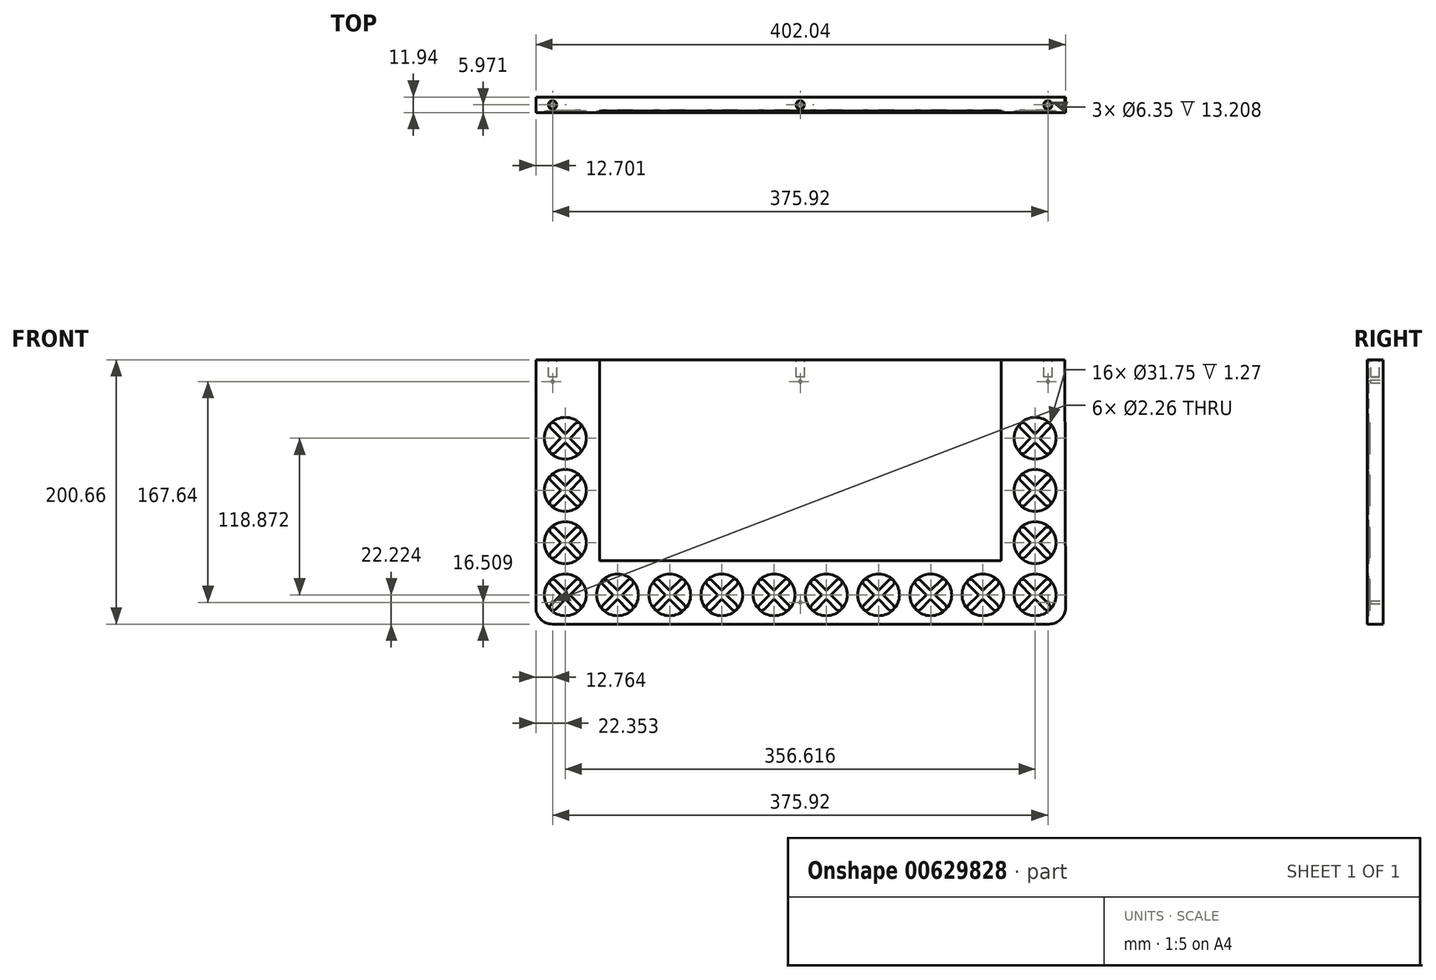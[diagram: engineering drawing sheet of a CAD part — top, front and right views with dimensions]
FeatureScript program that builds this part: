
annotation { "Feature Type Name" : "Feature", "Feature Type Description" : "" }
export const myFeature = defineFeature(function(context is Context, id is Id, definition is map)
    precondition{}
    {
        {
            var Q0;
            Q0=qCreatedBy(makeId("Front.planeOp"),FACE);
            var sketch = newSketch(context, id + "F0", { "sketchPlane" : qUnion([Q0])});
            skArc(sketch, "E0", {"start": v(-280, -77.67) * mm, "mid": v(-276.29, -86.65) * mm, "end": v(-267.3, -90.37) * mm});
            skArc(sketch, "E1", {"start": v(109.33, -90.37) * mm, "mid": v(118.3, -86.65) * mm, "end": v(122.03, -77.67) * mm});
            skLineSegment(sketch, "E2", {"start": v(121.31, 110.29) * mm, "end": v(122.03, -77.67) * mm});
            skLineSegment(sketch, "E3", {"start": v(109.33, -90.37) * mm, "end": v(-267.3, -90.37) * mm});
            skLineSegment(sketch, "E4", {"start": v(-280, 110.29) * mm, "end": v(-280, -77.67) * mm});
            skLineSegment(sketch, "E5", {"start": v(-280, 110.29) * mm, "end": v(121.31, 110.29) * mm});
            skSolve(sketch);
        }
        {
            var Q0;
            Q0=makeQuery(id+"F0.imprint","IMPRINT",FACE,{"disambiguationData":[TD([[makeQuery(id+"F0.imprint","IMPRINT",EDGE,{"derivedFrom":sQuery(id+"F0.wireOp",EDGE,"E0")}),1.0]])]});
            extrude(context, id + "F1", {"entities" : qUnion([Q0]), "depth" : 11.94 * mm, "offsetDistance" : 25.4 * mm});
        }
        {
            var Q0;
            Q0=makeQuery(id+"F1.opExtrude","SWEPT_FACE",FACE,{"disambiguationData":[OSD([sQuery(id+"F0.wireOp",EDGE,"E5")])]});
            var sketch = newSketch(context, id + "F2", { "sketchPlane" : qUnion([Q0])});
            skCircle(sketch, "E6", {"center": v(-267.3, -5.97) * mm, "radius": 3.18 * mm});
            skCircle(sketch, "E7", {"center": v(-79.35, -5.97) * mm, "radius": 3.18 * mm});
            skCircle(sketch, "E8", {"center": v(108.61, -5.97) * mm, "radius": 3.18 * mm});
            skSolve(sketch);
        }
        {
            var Q0;
            Q0=makeQuery(id+"F2.imprint","IMPRINT",FACE,{"disambiguationData":[TD([[makeQuery(id+"F2.imprint","IMPRINT",EDGE,{"derivedFrom":sQuery(id+"F2.wireOp",EDGE,"E6")}),1.0]])]});
            var Q1;
            Q1=makeQuery(id+"F2.imprint","IMPRINT",FACE,{"disambiguationData":[TD([[makeQuery(id+"F2.imprint","IMPRINT",EDGE,{"derivedFrom":sQuery(id+"F2.wireOp",EDGE,"E7")}),1.0]])]});
            var Q2;
            Q2=makeQuery(id+"F2.imprint","IMPRINT",FACE,{"disambiguationData":[TD([[makeQuery(id+"F2.imprint","IMPRINT",EDGE,{"derivedFrom":sQuery(id+"F2.wireOp",EDGE,"E8")}),1.0]])]});
            extrude(context, id + "F3", {"entities" : qUnion([Q0, Q1, Q2]), "operationType" : NewBodyOperationType.REMOVE, "oppositeDirection" : true, "depth" : 13.2 * mm, "offsetDistance" : 25.4 * mm});
        }
        {
            var Q0;
            Q0=makeQuery(id+"F1.opExtrude","CAP_FACE",FACE,{"disambiguationData":[OSD([sQuery(id+"F0.wireOp",EDGE,"E0"),sQuery(id+"F0.wireOp",EDGE,"E1"),sQuery(id+"F0.wireOp",EDGE,"E2"),sQuery(id+"F0.wireOp",EDGE,"E3"),sQuery(id+"F0.wireOp",EDGE,"E4"),sQuery(id+"F0.wireOp",EDGE,"E5")])],"isStart":true});
            var sketch = newSketch(context, id + "F4", { "sketchPlane" : qUnion([Q0])});
            skPoint(sketch, "E9", {"position": v(-108.67, 93.78) * mm});
            skPoint(sketch, "E10", {"position": v(267.25, -73.86) * mm});
            skPoint(sketch, "E11", {"position": v(79.29, 93.78) * mm});
            skPoint(sketch, "E12", {"position": v(-108.67, -73.86) * mm});
            skPoint(sketch, "E13", {"position": v(267.25, 93.78) * mm});
            skPoint(sketch, "E14", {"position": v(79.29, -73.86) * mm});
            skSolve(sketch);
        }
        {
            var Q0;
            Q0=sQuery(id+"F4.wireOp",VERTEX,"E9");
            var Q1;
            Q1=sQuery(id+"F4.wireOp",VERTEX,"E11");
            var Q2;
            Q2=sQuery(id+"F4.wireOp",VERTEX,"E13");
            var Q3;
            Q3=sQuery(id+"F4.wireOp",VERTEX,"E10");
            var Q4;
            Q4=sQuery(id+"F4.wireOp",VERTEX,"E14");
            var Q5;
            Q5=sQuery(id+"F4.wireOp",VERTEX,"E12");
            var Q6;
            Q6=makeQuery(id+"F1.opExtrude","SWEPT_BODY",BODY,{"disambiguationData":[OSD([sQuery(id+"F0.wireOp",EDGE,"E0"),sQuery(id+"F0.wireOp",EDGE,"E1"),sQuery(id+"F0.wireOp",EDGE,"E2"),sQuery(id+"F0.wireOp",EDGE,"E3"),sQuery(id+"F0.wireOp",EDGE,"E4"),sQuery(id+"F0.wireOp",EDGE,"E5")])]});
            hole(context, id + "F5", {"style" : HoleStyle.SIMPLE, "endStyle" : HoleEndStyle.BLIND, "standardTappedOrClearance" : lookupTablePath({ "standard" : "ANSI", "engagement" : "75%", "pitch" : "40 tpi", "size" : "#4", "type" : "Tapped" }), "standardBlindInLast" : lookupTablePath({ "standard" : "ANSI", "engagement" : "75%", "pitch" : "40 tpi", "size" : "#4", "type" : "Tapped" }), "holeDiameter" : 2.26 * mm, "showTappedDepth" : true, "holeDepth" : 9.52 * mm, "tappedDepth" : 7.62 * mm, "tapClearance" : 3, "locations" : qUnion([Q0, Q1, Q2, Q3, Q4, Q5]), "scope" : qUnion([Q6]), "majorDiameter" : 2.84 * mm});
        }
        {
            var Q0;
            Q0=makeQuery(id+"F1.opExtrude","CAP_FACE",FACE,{"disambiguationData":[OSD([sQuery(id+"F0.wireOp",EDGE,"E0"),sQuery(id+"F0.wireOp",EDGE,"E1"),sQuery(id+"F0.wireOp",EDGE,"E2"),sQuery(id+"F0.wireOp",EDGE,"E3"),sQuery(id+"F0.wireOp",EDGE,"E4"),sQuery(id+"F0.wireOp",EDGE,"E5")])],"isStart":false});
            var sketch = newSketch(context, id + "F6", { "sketchPlane" : qUnion([Q0])});
            skLineSegment(sketch, "E15.bottom", {"start": v(-231.75, 110.29) * mm, "end": v(73.05, 110.29) * mm});
            skArc(sketch, "E16", {"start": v(-231.75, -41.71) * mm, "mid": v(-231.63, -42) * mm, "end": v(-231.35, -42.11) * mm});
            skArc(sketch, "E17", {"start": v(72.65, -42.11) * mm, "mid": v(72.94, -42) * mm, "end": v(73.05, -41.71) * mm});
            skLineSegment(sketch, "E18", {"start": v(72.65, -42.11) * mm, "end": v(-231.35, -42.11) * mm});
            skLineSegment(sketch, "E19", {"start": v(-231.75, -41.71) * mm, "end": v(-231.75, 110.29) * mm});
            skLineSegment(sketch, "E20", {"start": v(73.05, 110.29) * mm, "end": v(73.05, -41.71) * mm});
            skSolve(sketch);
        }
        {
            var Q0;
            Q0=makeQuery(id+"F6.imprint","IMPRINT",FACE,{"disambiguationData":[TD([[makeQuery(id+"F6.imprint","IMPRINT",EDGE,{"derivedFrom":sQuery(id+"F6.wireOp",EDGE,"E15.bottom")}),-1.0]])]});
            extrude(context, id + "F7", {"entities" : qUnion([Q0]), "operationType" : NewBodyOperationType.REMOVE, "oppositeDirection" : true, "depth" : 1.27 * mm, "offsetDistance" : 25.4 * mm});
        }
        {
            var Q0;
            Q0=makeQuery(id+"F1.opExtrude","CAP_FACE",FACE,{"disambiguationData":[OSD([sQuery(id+"F0.wireOp",EDGE,"E0"),sQuery(id+"F0.wireOp",EDGE,"E1"),sQuery(id+"F0.wireOp",EDGE,"E2"),sQuery(id+"F0.wireOp",EDGE,"E3"),sQuery(id+"F0.wireOp",EDGE,"E4"),sQuery(id+"F0.wireOp",EDGE,"E5")])],"isStart":false});
            var sketch = newSketch(context, id + "F8", { "sketchPlane" : qUnion([Q0])});
            skCircle(sketch, "E21", {"center": v(-257.66, -68.15) * mm, "radius": 15.88 * mm});
            skCircle(sketch, "E22.1.0.0", {"center": v(-218.03, -68.15) * mm, "radius": 15.88 * mm});
            skCircle(sketch, "E22.2.0.0", {"center": v(-178.4, -68.15) * mm, "radius": 15.88 * mm});
            skCircle(sketch, "E22.3.0.0", {"center": v(-138.78, -68.15) * mm, "radius": 15.88 * mm});
            skCircle(sketch, "E22.4.0.0", {"center": v(-99.16, -68.15) * mm, "radius": 15.88 * mm});
            skCircle(sketch, "E22.5.0.0", {"center": v(-59.54, -68.15) * mm, "radius": 15.88 * mm});
            skCircle(sketch, "E22.6.0.0", {"center": v(-19.91, -68.15) * mm, "radius": 15.88 * mm});
            skCircle(sketch, "E22.7.0.0", {"center": v(19.71, -68.15) * mm, "radius": 15.88 * mm});
            skCircle(sketch, "E22.8.0.0", {"center": v(59.34, -68.15) * mm, "radius": 15.88 * mm});
            skCircle(sketch, "E22.9.0.0", {"center": v(98.96, -68.15) * mm, "radius": 15.88 * mm});
            skCircle(sketch, "E23.0.1.0", {"center": v(-257.66, -28.52) * mm, "radius": 15.88 * mm});
            skCircle(sketch, "E23.0.1.1", {"center": v(98.96, -28.52) * mm, "radius": 15.88 * mm});
            skCircle(sketch, "E23.0.2.0", {"center": v(-257.66, 11.1) * mm, "radius": 15.88 * mm});
            skCircle(sketch, "E23.0.2.1", {"center": v(98.96, 11.1) * mm, "radius": 15.88 * mm});
            skCircle(sketch, "E23.0.3.0", {"center": v(-257.66, 50.73) * mm, "radius": 15.88 * mm});
            skCircle(sketch, "E23.0.3.1", {"center": v(98.96, 50.73) * mm, "radius": 15.88 * mm});
            skSolve(sketch);
        }
        {
            var Q0;
            Q0=qSketchRegion(id+"F8",true);
            extrude(context, id + "F9", {"entities" : qUnion([Q0]), "operationType" : NewBodyOperationType.REMOVE, "oppositeDirection" : true, "depth" : 1.27 * mm, "offsetDistance" : 25.4 * mm});
        }
        {
            var Q0;
            Q0=makeQuery(id+"F1.opExtrude","CAP_FACE",FACE,{"disambiguationData":[OSD([sQuery(id+"F0.wireOp",EDGE,"E0"),sQuery(id+"F0.wireOp",EDGE,"E1"),sQuery(id+"F0.wireOp",EDGE,"E2"),sQuery(id+"F0.wireOp",EDGE,"E3"),sQuery(id+"F0.wireOp",EDGE,"E4"),sQuery(id+"F0.wireOp",EDGE,"E5")])],"isStart":false});
            var sketch = newSketch(context, id + "F10", { "sketchPlane" : qUnion([Q0])});
            skArc(sketch, "E24", {"start": v(-249.98, -79.24) * mm, "mid": v(-246.61, -79.37) * mm, "end": v(-246.48, -76) * mm});
            skArc(sketch, "E25", {"start": v(-265.42, -57.06) * mm, "mid": v(-268.8, -57.06) * mm, "end": v(-268.8, -60.42) * mm});
            skLineSegment(sketch, "E26.bottom", {"start": v(-254.2, -68.28) * mm, "end": v(-246.48, -60.56) * mm});
            skLineSegment(sketch, "E26.top", {"start": v(-257.7, -64.78) * mm, "end": v(-249.98, -57.06) * mm});
            skLineSegment(sketch, "E27.bottom", {"start": v(-257.7, -71.52) * mm, "end": v(-265.42, -79.24) * mm});
            skArc(sketch, "E28", {"start": v(-246.48, -60.56) * mm, "mid": v(-246.48, -57.06) * mm, "end": v(-249.98, -57.06) * mm});
            skArc(sketch, "E29", {"start": v(-268.8, -75.87) * mm, "mid": v(-268.8, -79.24) * mm, "end": v(-265.42, -79.24) * mm});
            skLineSegment(sketch, "E30.0", {"start": v(-249.98, -57.06) * mm, "end": v(-257.7, -64.78) * mm, "construction": true});
            skLineSegment(sketch, "E31", {"start": v(-268.8, -60.42) * mm, "end": v(-261.07, -68.15) * mm});
            skLineSegment(sketch, "E32", {"start": v(-265.42, -57.06) * mm, "end": v(-257.7, -64.78) * mm});
            skLineSegment(sketch, "E33", {"start": v(-254.2, -68.28) * mm, "end": v(-246.48, -76) * mm});
            skLineSegment(sketch, "E34", {"start": v(-249.98, -79.24) * mm, "end": v(-257.7, -71.52) * mm});
            skLineSegment(sketch, "E35", {"start": v(-261.07, -68.15) * mm, "end": v(-268.8, -75.87) * mm});
            skLineSegment(sketch, "E36.0", {"start": v(-251.89, -73.92) * mm, "end": v(-251.89, -73.92) * mm});
            skLineSegment(sketch, "E36.9", {"start": v(-251.89, -73.92) * mm, "end": v(-251.89, -73.92) * mm});
            skLineSegment(sketch, "E37.0", {"start": v(-257.7, -71.52) * mm, "end": v(-249.98, -79.24) * mm, "construction": true});
            skLineSegment(sketch, "E38.0", {"start": v(-254.2, -68.28) * mm, "end": v(-246.48, -76) * mm, "construction": true});
            skLineSegment(sketch, "E39.0", {"start": v(-268.8, -60.42) * mm, "end": v(-261.07, -68.15) * mm, "construction": true});
            skLineSegment(sketch, "E40.0", {"start": v(-265.42, -79.24) * mm, "end": v(-257.7, -71.52) * mm, "construction": true});
            skLineSegment(sketch, "E41.0", {"start": v(-268.8, -75.87) * mm, "end": v(-261.07, -68.15) * mm, "construction": true});
            skArc(sketch, "E42.0.0.1", {"start": v(-265.42, -17.43) * mm, "mid": v(-268.8, -17.43) * mm, "end": v(-268.8, -20.8) * mm});
            skLineSegment(sketch, "E42.4.0.1", {"start": v(-254.2, -28.66) * mm, "end": v(-246.48, -20.94) * mm});
            skLineSegment(sketch, "E42.7.0.1", {"start": v(-265.42, -17.43) * mm, "end": v(-257.7, -25.16) * mm});
            skLineSegment(sketch, "E42.10.0.1", {"start": v(-268.8, -36.25) * mm, "end": v(-261.07, -28.52) * mm, "construction": true});
            skLineSegment(sketch, "E42.13.0.1", {"start": v(-257.7, -31.9) * mm, "end": v(-249.98, -39.61) * mm, "construction": true});
            skLineSegment(sketch, "E42.16.0.1", {"start": v(-254.2, -28.66) * mm, "end": v(-246.48, -36.38) * mm, "construction": true});
            skLineSegment(sketch, "E42.19.0.1", {"start": v(-268.8, -20.8) * mm, "end": v(-261.07, -28.52) * mm, "construction": true});
            skArc(sketch, "E42.22.0.1", {"start": v(-249.98, -39.61) * mm, "mid": v(-246.61, -39.75) * mm, "end": v(-246.48, -36.38) * mm});
            skArc(sketch, "E42.26.0.1", {"start": v(-246.48, -20.94) * mm, "mid": v(-246.48, -17.43) * mm, "end": v(-249.98, -17.43) * mm});
            skLineSegment(sketch, "E42.30.0.1", {"start": v(-249.98, -17.43) * mm, "end": v(-257.7, -25.16) * mm, "construction": true});
            skLineSegment(sketch, "E42.33.0.1", {"start": v(-265.42, -39.61) * mm, "end": v(-257.7, -31.9) * mm, "construction": true});
            skLineSegment(sketch, "E42.36.0.1", {"start": v(-257.7, -25.16) * mm, "end": v(-249.98, -17.43) * mm});
            skArc(sketch, "E42.39.0.1", {"start": v(-268.8, -36.25) * mm, "mid": v(-268.8, -39.61) * mm, "end": v(-265.42, -39.61) * mm});
            skLineSegment(sketch, "E42.43.0.1", {"start": v(-268.8, -20.8) * mm, "end": v(-261.07, -28.52) * mm});
            skLineSegment(sketch, "E42.46.0.1", {"start": v(-254.2, -28.66) * mm, "end": v(-246.48, -36.38) * mm});
            skLineSegment(sketch, "E42.49.0.1", {"start": v(-249.98, -39.61) * mm, "end": v(-257.7, -31.9) * mm});
            skLineSegment(sketch, "E42.52.0.1", {"start": v(-261.07, -28.52) * mm, "end": v(-268.8, -36.25) * mm});
            skLineSegment(sketch, "E42.55.0.1", {"start": v(-257.7, -31.9) * mm, "end": v(-265.42, -39.61) * mm});
            skArc(sketch, "E42.0.0.2", {"start": v(-265.42, 22.2) * mm, "mid": v(-268.8, 22.2) * mm, "end": v(-268.8, 18.82) * mm});
            skLineSegment(sketch, "E42.4.0.2", {"start": v(-254.2, 10.97) * mm, "end": v(-246.48, 18.69) * mm});
            skLineSegment(sketch, "E42.7.0.2", {"start": v(-265.42, 22.2) * mm, "end": v(-257.7, 14.47) * mm});
            skLineSegment(sketch, "E42.10.0.2", {"start": v(-268.8, 3.38) * mm, "end": v(-261.07, 11.1) * mm, "construction": true});
            skLineSegment(sketch, "E42.13.0.2", {"start": v(-257.7, 7.73) * mm, "end": v(-249.98, 0) * mm, "construction": true});
            skLineSegment(sketch, "E42.16.0.2", {"start": v(-254.2, 10.97) * mm, "end": v(-246.48, 3.24) * mm, "construction": true});
            skLineSegment(sketch, "E42.19.0.2", {"start": v(-268.8, 18.82) * mm, "end": v(-261.07, 11.1) * mm, "construction": true});
            skArc(sketch, "E42.22.0.2", {"start": v(-249.98, 0) * mm, "mid": v(-246.61, -0.13) * mm, "end": v(-246.48, 3.24) * mm});
            skArc(sketch, "E42.26.0.2", {"start": v(-246.48, 18.69) * mm, "mid": v(-246.48, 22.2) * mm, "end": v(-249.98, 22.2) * mm});
            skLineSegment(sketch, "E42.30.0.2", {"start": v(-249.98, 22.2) * mm, "end": v(-257.7, 14.47) * mm, "construction": true});
            skLineSegment(sketch, "E42.33.0.2", {"start": v(-265.42, 0) * mm, "end": v(-257.7, 7.73) * mm, "construction": true});
            skLineSegment(sketch, "E42.36.0.2", {"start": v(-257.7, 14.47) * mm, "end": v(-249.98, 22.2) * mm});
            skArc(sketch, "E42.39.0.2", {"start": v(-268.8, 3.38) * mm, "mid": v(-268.8, 0) * mm, "end": v(-265.42, 0) * mm});
            skLineSegment(sketch, "E42.43.0.2", {"start": v(-268.8, 18.82) * mm, "end": v(-261.07, 11.1) * mm});
            skLineSegment(sketch, "E42.46.0.2", {"start": v(-254.2, 10.97) * mm, "end": v(-246.48, 3.24) * mm});
            skLineSegment(sketch, "E42.49.0.2", {"start": v(-249.98, 0) * mm, "end": v(-257.7, 7.73) * mm});
            skLineSegment(sketch, "E42.52.0.2", {"start": v(-261.07, 11.1) * mm, "end": v(-268.8, 3.38) * mm});
            skLineSegment(sketch, "E42.55.0.2", {"start": v(-257.7, 7.73) * mm, "end": v(-265.42, 0) * mm});
            skArc(sketch, "E42.0.0.3", {"start": v(-265.42, 61.81) * mm, "mid": v(-268.8, 61.81) * mm, "end": v(-268.8, 58.45) * mm});
            skLineSegment(sketch, "E42.4.0.3", {"start": v(-254.2, 50.59) * mm, "end": v(-246.48, 58.31) * mm});
            skLineSegment(sketch, "E42.7.0.3", {"start": v(-265.42, 61.81) * mm, "end": v(-257.7, 54.1) * mm});
            skLineSegment(sketch, "E42.10.0.3", {"start": v(-268.8, 43) * mm, "end": v(-261.07, 50.72) * mm, "construction": true});
            skLineSegment(sketch, "E42.13.0.3", {"start": v(-257.7, 47.36) * mm, "end": v(-249.98, 39.63) * mm, "construction": true});
            skLineSegment(sketch, "E42.16.0.3", {"start": v(-254.2, 50.59) * mm, "end": v(-246.48, 42.87) * mm, "construction": true});
            skLineSegment(sketch, "E42.19.0.3", {"start": v(-268.8, 58.45) * mm, "end": v(-261.07, 50.72) * mm, "construction": true});
            skArc(sketch, "E42.22.0.3", {"start": v(-249.98, 39.63) * mm, "mid": v(-246.61, 39.5) * mm, "end": v(-246.48, 42.87) * mm});
            skArc(sketch, "E42.26.0.3", {"start": v(-246.48, 58.31) * mm, "mid": v(-246.48, 61.81) * mm, "end": v(-249.98, 61.81) * mm});
            skLineSegment(sketch, "E42.30.0.3", {"start": v(-249.98, 61.81) * mm, "end": v(-257.7, 54.1) * mm, "construction": true});
            skLineSegment(sketch, "E42.33.0.3", {"start": v(-265.42, 39.63) * mm, "end": v(-257.7, 47.36) * mm, "construction": true});
            skLineSegment(sketch, "E42.36.0.3", {"start": v(-257.7, 54.1) * mm, "end": v(-249.98, 61.81) * mm});
            skArc(sketch, "E42.39.0.3", {"start": v(-268.8, 43) * mm, "mid": v(-268.8, 39.63) * mm, "end": v(-265.42, 39.63) * mm});
            skLineSegment(sketch, "E42.43.0.3", {"start": v(-268.8, 58.45) * mm, "end": v(-261.07, 50.72) * mm});
            skLineSegment(sketch, "E42.46.0.3", {"start": v(-254.2, 50.59) * mm, "end": v(-246.48, 42.87) * mm});
            skLineSegment(sketch, "E42.49.0.3", {"start": v(-249.98, 39.63) * mm, "end": v(-257.7, 47.36) * mm});
            skLineSegment(sketch, "E42.52.0.3", {"start": v(-261.07, 50.72) * mm, "end": v(-268.8, 43) * mm});
            skLineSegment(sketch, "E42.55.0.3", {"start": v(-257.7, 47.36) * mm, "end": v(-265.42, 39.63) * mm});
            skArc(sketch, "E43.0.1.0", {"start": v(-229.17, -75.87) * mm, "mid": v(-229.17, -79.24) * mm, "end": v(-225.8, -79.24) * mm});
            skArc(sketch, "E43.4.1.0", {"start": v(-225.8, -57.06) * mm, "mid": v(-229.17, -57.06) * mm, "end": v(-229.17, -60.42) * mm});
            skLineSegment(sketch, "E43.8.1.0", {"start": v(-214.57, -68.28) * mm, "end": v(-206.85, -76) * mm, "construction": true});
            skLineSegment(sketch, "E43.11.1.0", {"start": v(-218.08, -71.52) * mm, "end": v(-210.35, -79.24) * mm, "construction": true});
            skLineSegment(sketch, "E43.14.1.0", {"start": v(-225.8, -79.24) * mm, "end": v(-218.08, -71.52) * mm, "construction": true});
            skArc(sketch, "E43.17.1.0", {"start": v(-210.35, -79.24) * mm, "mid": v(-206.99, -79.37) * mm, "end": v(-206.85, -76) * mm});
            skArc(sketch, "E43.21.1.0", {"start": v(-206.85, -60.56) * mm, "mid": v(-206.85, -57.06) * mm, "end": v(-210.35, -57.06) * mm});
            skLineSegment(sketch, "E43.25.1.0", {"start": v(-214.57, -68.28) * mm, "end": v(-206.85, -60.56) * mm});
            skLineSegment(sketch, "E43.28.1.0", {"start": v(-229.17, -75.87) * mm, "end": v(-221.44, -68.15) * mm, "construction": true});
            skLineSegment(sketch, "E43.31.1.0", {"start": v(-229.17, -60.42) * mm, "end": v(-221.44, -68.15) * mm, "construction": true});
            skLineSegment(sketch, "E43.34.1.0", {"start": v(-225.8, -57.06) * mm, "end": v(-218.08, -64.78) * mm});
            skLineSegment(sketch, "E43.37.1.0", {"start": v(-210.35, -57.06) * mm, "end": v(-218.08, -64.78) * mm, "construction": true});
            skLineSegment(sketch, "E43.40.1.0", {"start": v(-210.35, -79.24) * mm, "end": v(-218.08, -71.52) * mm});
            skLineSegment(sketch, "E43.43.1.0", {"start": v(-214.57, -68.28) * mm, "end": v(-206.85, -76) * mm});
            skLineSegment(sketch, "E43.46.1.0", {"start": v(-218.08, -64.78) * mm, "end": v(-210.35, -57.06) * mm});
            skLineSegment(sketch, "E43.49.1.0", {"start": v(-221.44, -68.15) * mm, "end": v(-229.17, -75.87) * mm});
            skLineSegment(sketch, "E43.52.1.0", {"start": v(-229.17, -60.42) * mm, "end": v(-221.44, -68.15) * mm});
            skLineSegment(sketch, "E43.55.1.0", {"start": v(-218.08, -71.52) * mm, "end": v(-225.8, -79.24) * mm});
            skArc(sketch, "E43.0.2.0", {"start": v(-189.54, -75.87) * mm, "mid": v(-189.54, -79.24) * mm, "end": v(-186.18, -79.24) * mm});
            skArc(sketch, "E43.4.2.0", {"start": v(-186.18, -57.06) * mm, "mid": v(-189.54, -57.06) * mm, "end": v(-189.54, -60.42) * mm});
            skLineSegment(sketch, "E43.8.2.0", {"start": v(-174.95, -68.28) * mm, "end": v(-167.23, -76) * mm, "construction": true});
            skLineSegment(sketch, "E43.11.2.0", {"start": v(-178.45, -71.52) * mm, "end": v(-170.73, -79.24) * mm, "construction": true});
            skLineSegment(sketch, "E43.14.2.0", {"start": v(-186.18, -79.24) * mm, "end": v(-178.45, -71.52) * mm, "construction": true});
            skArc(sketch, "E43.17.2.0", {"start": v(-170.73, -79.24) * mm, "mid": v(-167.36, -79.37) * mm, "end": v(-167.23, -76) * mm});
            skArc(sketch, "E43.21.2.0", {"start": v(-167.23, -60.56) * mm, "mid": v(-167.23, -57.06) * mm, "end": v(-170.73, -57.06) * mm});
            skLineSegment(sketch, "E43.25.2.0", {"start": v(-174.95, -68.28) * mm, "end": v(-167.23, -60.56) * mm});
            skLineSegment(sketch, "E43.28.2.0", {"start": v(-189.54, -75.87) * mm, "end": v(-181.82, -68.15) * mm, "construction": true});
            skLineSegment(sketch, "E43.31.2.0", {"start": v(-189.54, -60.42) * mm, "end": v(-181.82, -68.15) * mm, "construction": true});
            skLineSegment(sketch, "E43.34.2.0", {"start": v(-186.18, -57.06) * mm, "end": v(-178.45, -64.78) * mm});
            skLineSegment(sketch, "E43.37.2.0", {"start": v(-170.73, -57.06) * mm, "end": v(-178.45, -64.78) * mm, "construction": true});
            skLineSegment(sketch, "E43.40.2.0", {"start": v(-170.73, -79.24) * mm, "end": v(-178.45, -71.52) * mm});
            skLineSegment(sketch, "E43.43.2.0", {"start": v(-174.95, -68.28) * mm, "end": v(-167.23, -76) * mm});
            skLineSegment(sketch, "E43.46.2.0", {"start": v(-178.45, -64.78) * mm, "end": v(-170.73, -57.06) * mm});
            skLineSegment(sketch, "E43.49.2.0", {"start": v(-181.82, -68.15) * mm, "end": v(-189.54, -75.87) * mm});
            skLineSegment(sketch, "E43.52.2.0", {"start": v(-189.54, -60.42) * mm, "end": v(-181.82, -68.15) * mm});
            skLineSegment(sketch, "E43.55.2.0", {"start": v(-178.45, -71.52) * mm, "end": v(-186.18, -79.24) * mm});
            skArc(sketch, "E43.0.3.0", {"start": v(-149.92, -75.87) * mm, "mid": v(-149.92, -79.24) * mm, "end": v(-146.55, -79.24) * mm});
            skArc(sketch, "E43.4.3.0", {"start": v(-146.55, -57.06) * mm, "mid": v(-149.92, -57.06) * mm, "end": v(-149.92, -60.42) * mm});
            skLineSegment(sketch, "E43.8.3.0", {"start": v(-135.33, -68.28) * mm, "end": v(-127.6, -76) * mm, "construction": true});
            skLineSegment(sketch, "E43.11.3.0", {"start": v(-138.83, -71.52) * mm, "end": v(-131.1, -79.24) * mm, "construction": true});
            skLineSegment(sketch, "E43.14.3.0", {"start": v(-146.55, -79.24) * mm, "end": v(-138.83, -71.52) * mm, "construction": true});
            skArc(sketch, "E43.17.3.0", {"start": v(-131.1, -79.24) * mm, "mid": v(-127.74, -79.37) * mm, "end": v(-127.6, -76) * mm});
            skArc(sketch, "E43.21.3.0", {"start": v(-127.6, -60.56) * mm, "mid": v(-127.6, -57.06) * mm, "end": v(-131.1, -57.06) * mm});
            skLineSegment(sketch, "E43.25.3.0", {"start": v(-135.33, -68.28) * mm, "end": v(-127.6, -60.56) * mm});
            skLineSegment(sketch, "E43.28.3.0", {"start": v(-149.92, -75.87) * mm, "end": v(-142.2, -68.15) * mm, "construction": true});
            skLineSegment(sketch, "E43.31.3.0", {"start": v(-149.92, -60.42) * mm, "end": v(-142.2, -68.15) * mm, "construction": true});
            skLineSegment(sketch, "E43.34.3.0", {"start": v(-146.55, -57.06) * mm, "end": v(-138.83, -64.78) * mm});
            skLineSegment(sketch, "E43.37.3.0", {"start": v(-131.1, -57.06) * mm, "end": v(-138.83, -64.78) * mm, "construction": true});
            skLineSegment(sketch, "E43.40.3.0", {"start": v(-131.1, -79.24) * mm, "end": v(-138.83, -71.52) * mm});
            skLineSegment(sketch, "E43.43.3.0", {"start": v(-135.33, -68.28) * mm, "end": v(-127.6, -76) * mm});
            skLineSegment(sketch, "E43.46.3.0", {"start": v(-138.83, -64.78) * mm, "end": v(-131.1, -57.06) * mm});
            skLineSegment(sketch, "E43.49.3.0", {"start": v(-142.2, -68.15) * mm, "end": v(-149.92, -75.87) * mm});
            skLineSegment(sketch, "E43.52.3.0", {"start": v(-149.92, -60.42) * mm, "end": v(-142.2, -68.15) * mm});
            skLineSegment(sketch, "E43.55.3.0", {"start": v(-138.83, -71.52) * mm, "end": v(-146.55, -79.24) * mm});
            skArc(sketch, "E43.0.4.0", {"start": v(-110.3, -75.87) * mm, "mid": v(-110.3, -79.24) * mm, "end": v(-106.93, -79.24) * mm});
            skArc(sketch, "E43.4.4.0", {"start": v(-106.93, -57.06) * mm, "mid": v(-110.3, -57.06) * mm, "end": v(-110.3, -60.42) * mm});
            skLineSegment(sketch, "E43.8.4.0", {"start": v(-95.7, -68.28) * mm, "end": v(-87.98, -76) * mm, "construction": true});
            skLineSegment(sketch, "E43.11.4.0", {"start": v(-99.2, -71.52) * mm, "end": v(-91.48, -79.24) * mm, "construction": true});
            skLineSegment(sketch, "E43.14.4.0", {"start": v(-106.93, -79.24) * mm, "end": v(-99.2, -71.52) * mm, "construction": true});
            skArc(sketch, "E43.17.4.0", {"start": v(-91.48, -79.24) * mm, "mid": v(-88.11, -79.37) * mm, "end": v(-87.98, -76) * mm});
            skArc(sketch, "E43.21.4.0", {"start": v(-87.98, -60.56) * mm, "mid": v(-87.98, -57.06) * mm, "end": v(-91.48, -57.06) * mm});
            skLineSegment(sketch, "E43.25.4.0", {"start": v(-95.7, -68.28) * mm, "end": v(-87.98, -60.56) * mm});
            skLineSegment(sketch, "E43.28.4.0", {"start": v(-110.3, -75.87) * mm, "end": v(-102.57, -68.15) * mm, "construction": true});
            skLineSegment(sketch, "E43.31.4.0", {"start": v(-110.3, -60.42) * mm, "end": v(-102.57, -68.15) * mm, "construction": true});
            skLineSegment(sketch, "E43.34.4.0", {"start": v(-106.93, -57.06) * mm, "end": v(-99.2, -64.78) * mm});
            skLineSegment(sketch, "E43.37.4.0", {"start": v(-91.48, -57.06) * mm, "end": v(-99.2, -64.78) * mm, "construction": true});
            skLineSegment(sketch, "E43.40.4.0", {"start": v(-91.48, -79.24) * mm, "end": v(-99.2, -71.52) * mm});
            skLineSegment(sketch, "E43.43.4.0", {"start": v(-95.7, -68.28) * mm, "end": v(-87.98, -76) * mm});
            skLineSegment(sketch, "E43.46.4.0", {"start": v(-99.2, -64.78) * mm, "end": v(-91.48, -57.06) * mm});
            skLineSegment(sketch, "E43.49.4.0", {"start": v(-102.57, -68.15) * mm, "end": v(-110.3, -75.87) * mm});
            skLineSegment(sketch, "E43.52.4.0", {"start": v(-110.3, -60.42) * mm, "end": v(-102.57, -68.15) * mm});
            skLineSegment(sketch, "E43.55.4.0", {"start": v(-99.2, -71.52) * mm, "end": v(-106.93, -79.24) * mm});
            skArc(sketch, "E43.0.5.0", {"start": v(-70.67, -75.87) * mm, "mid": v(-70.67, -79.24) * mm, "end": v(-67.3, -79.24) * mm});
            skArc(sketch, "E43.4.5.0", {"start": v(-67.3, -57.06) * mm, "mid": v(-70.67, -57.06) * mm, "end": v(-70.67, -60.42) * mm});
            skLineSegment(sketch, "E43.8.5.0", {"start": v(-56.08, -68.28) * mm, "end": v(-48.36, -76) * mm, "construction": true});
            skLineSegment(sketch, "E43.11.5.0", {"start": v(-59.58, -71.52) * mm, "end": v(-51.86, -79.24) * mm, "construction": true});
            skLineSegment(sketch, "E43.14.5.0", {"start": v(-67.3, -79.24) * mm, "end": v(-59.58, -71.52) * mm, "construction": true});
            skArc(sketch, "E43.17.5.0", {"start": v(-51.86, -79.24) * mm, "mid": v(-48.5, -79.37) * mm, "end": v(-48.36, -76) * mm});
            skArc(sketch, "E43.21.5.0", {"start": v(-48.36, -60.56) * mm, "mid": v(-48.36, -57.06) * mm, "end": v(-51.86, -57.06) * mm});
            skLineSegment(sketch, "E43.25.5.0", {"start": v(-56.08, -68.28) * mm, "end": v(-48.36, -60.56) * mm});
            skLineSegment(sketch, "E43.28.5.0", {"start": v(-70.67, -75.87) * mm, "end": v(-62.95, -68.15) * mm, "construction": true});
            skLineSegment(sketch, "E43.31.5.0", {"start": v(-70.67, -60.42) * mm, "end": v(-62.95, -68.15) * mm, "construction": true});
            skLineSegment(sketch, "E43.34.5.0", {"start": v(-67.3, -57.06) * mm, "end": v(-59.58, -64.78) * mm});
            skLineSegment(sketch, "E43.37.5.0", {"start": v(-51.86, -57.06) * mm, "end": v(-59.58, -64.78) * mm, "construction": true});
            skLineSegment(sketch, "E43.40.5.0", {"start": v(-51.86, -79.24) * mm, "end": v(-59.58, -71.52) * mm});
            skLineSegment(sketch, "E43.43.5.0", {"start": v(-56.08, -68.28) * mm, "end": v(-48.36, -76) * mm});
            skLineSegment(sketch, "E43.46.5.0", {"start": v(-59.58, -64.78) * mm, "end": v(-51.86, -57.06) * mm});
            skLineSegment(sketch, "E43.49.5.0", {"start": v(-62.95, -68.15) * mm, "end": v(-70.67, -75.87) * mm});
            skLineSegment(sketch, "E43.52.5.0", {"start": v(-70.67, -60.42) * mm, "end": v(-62.95, -68.15) * mm});
            skLineSegment(sketch, "E43.55.5.0", {"start": v(-59.58, -71.52) * mm, "end": v(-67.3, -79.24) * mm});
            skArc(sketch, "E43.0.6.0", {"start": v(-31.05, -75.87) * mm, "mid": v(-31.05, -79.24) * mm, "end": v(-27.68, -79.24) * mm});
            skArc(sketch, "E43.4.6.0", {"start": v(-27.68, -57.06) * mm, "mid": v(-31.05, -57.06) * mm, "end": v(-31.05, -60.42) * mm});
            skLineSegment(sketch, "E43.8.6.0", {"start": v(-16.45, -68.28) * mm, "end": v(-8.73, -76) * mm, "construction": true});
            skLineSegment(sketch, "E43.11.6.0", {"start": v(-19.96, -71.52) * mm, "end": v(-12.23, -79.24) * mm, "construction": true});
            skLineSegment(sketch, "E43.14.6.0", {"start": v(-27.68, -79.24) * mm, "end": v(-19.96, -71.52) * mm, "construction": true});
            skArc(sketch, "E43.17.6.0", {"start": v(-12.23, -79.24) * mm, "mid": v(-8.87, -79.37) * mm, "end": v(-8.73, -76) * mm});
            skArc(sketch, "E43.21.6.0", {"start": v(-8.73, -60.56) * mm, "mid": v(-8.73, -57.06) * mm, "end": v(-12.23, -57.06) * mm});
            skLineSegment(sketch, "E43.25.6.0", {"start": v(-16.45, -68.28) * mm, "end": v(-8.73, -60.56) * mm});
            skLineSegment(sketch, "E43.28.6.0", {"start": v(-31.05, -75.87) * mm, "end": v(-23.32, -68.15) * mm, "construction": true});
            skLineSegment(sketch, "E43.31.6.0", {"start": v(-31.05, -60.42) * mm, "end": v(-23.32, -68.15) * mm, "construction": true});
            skLineSegment(sketch, "E43.34.6.0", {"start": v(-27.68, -57.06) * mm, "end": v(-19.96, -64.78) * mm});
            skLineSegment(sketch, "E43.37.6.0", {"start": v(-12.23, -57.06) * mm, "end": v(-19.96, -64.78) * mm, "construction": true});
            skLineSegment(sketch, "E43.40.6.0", {"start": v(-12.23, -79.24) * mm, "end": v(-19.96, -71.52) * mm});
            skLineSegment(sketch, "E43.43.6.0", {"start": v(-16.45, -68.28) * mm, "end": v(-8.73, -76) * mm});
            skLineSegment(sketch, "E43.46.6.0", {"start": v(-19.96, -64.78) * mm, "end": v(-12.23, -57.06) * mm});
            skLineSegment(sketch, "E43.49.6.0", {"start": v(-23.32, -68.15) * mm, "end": v(-31.05, -75.87) * mm});
            skLineSegment(sketch, "E43.52.6.0", {"start": v(-31.05, -60.42) * mm, "end": v(-23.32, -68.15) * mm});
            skLineSegment(sketch, "E43.55.6.0", {"start": v(-19.96, -71.52) * mm, "end": v(-27.68, -79.24) * mm});
            skArc(sketch, "E43.0.7.0", {"start": v(8.58, -75.87) * mm, "mid": v(8.58, -79.24) * mm, "end": v(11.94, -79.24) * mm});
            skArc(sketch, "E43.4.7.0", {"start": v(11.94, -57.06) * mm, "mid": v(8.58, -57.06) * mm, "end": v(8.58, -60.42) * mm});
            skLineSegment(sketch, "E43.8.7.0", {"start": v(23.17, -68.28) * mm, "end": v(30.9, -76) * mm, "construction": true});
            skLineSegment(sketch, "E43.11.7.0", {"start": v(19.67, -71.52) * mm, "end": v(27.39, -79.24) * mm, "construction": true});
            skLineSegment(sketch, "E43.14.7.0", {"start": v(11.94, -79.24) * mm, "end": v(19.67, -71.52) * mm, "construction": true});
            skArc(sketch, "E43.17.7.0", {"start": v(27.39, -79.24) * mm, "mid": v(30.76, -79.37) * mm, "end": v(30.9, -76) * mm});
            skArc(sketch, "E43.21.7.0", {"start": v(30.9, -60.56) * mm, "mid": v(30.9, -57.06) * mm, "end": v(27.39, -57.06) * mm});
            skLineSegment(sketch, "E43.25.7.0", {"start": v(23.17, -68.28) * mm, "end": v(30.9, -60.56) * mm});
            skLineSegment(sketch, "E43.28.7.0", {"start": v(8.58, -75.87) * mm, "end": v(16.3, -68.15) * mm, "construction": true});
            skLineSegment(sketch, "E43.31.7.0", {"start": v(8.58, -60.42) * mm, "end": v(16.3, -68.15) * mm, "construction": true});
            skLineSegment(sketch, "E43.34.7.0", {"start": v(11.94, -57.06) * mm, "end": v(19.67, -64.78) * mm});
            skLineSegment(sketch, "E43.37.7.0", {"start": v(27.39, -57.06) * mm, "end": v(19.67, -64.78) * mm, "construction": true});
            skLineSegment(sketch, "E43.40.7.0", {"start": v(27.39, -79.24) * mm, "end": v(19.67, -71.52) * mm});
            skLineSegment(sketch, "E43.43.7.0", {"start": v(23.17, -68.28) * mm, "end": v(30.9, -76) * mm});
            skLineSegment(sketch, "E43.46.7.0", {"start": v(19.67, -64.78) * mm, "end": v(27.39, -57.06) * mm});
            skLineSegment(sketch, "E43.49.7.0", {"start": v(16.3, -68.15) * mm, "end": v(8.58, -75.87) * mm});
            skLineSegment(sketch, "E43.52.7.0", {"start": v(8.58, -60.42) * mm, "end": v(16.3, -68.15) * mm});
            skLineSegment(sketch, "E43.55.7.0", {"start": v(19.67, -71.52) * mm, "end": v(11.94, -79.24) * mm});
            skArc(sketch, "E43.0.8.0", {"start": v(48.2, -75.87) * mm, "mid": v(48.2, -79.24) * mm, "end": v(51.57, -79.24) * mm});
            skArc(sketch, "E43.4.8.0", {"start": v(51.57, -57.06) * mm, "mid": v(48.2, -57.06) * mm, "end": v(48.2, -60.42) * mm});
            skLineSegment(sketch, "E43.8.8.0", {"start": v(62.8, -68.28) * mm, "end": v(70.52, -76) * mm, "construction": true});
            skLineSegment(sketch, "E43.11.8.0", {"start": v(59.3, -71.52) * mm, "end": v(67.01, -79.24) * mm, "construction": true});
            skLineSegment(sketch, "E43.14.8.0", {"start": v(51.57, -79.24) * mm, "end": v(59.3, -71.52) * mm, "construction": true});
            skArc(sketch, "E43.17.8.0", {"start": v(67.01, -79.24) * mm, "mid": v(70.38, -79.37) * mm, "end": v(70.52, -76) * mm});
            skArc(sketch, "E43.21.8.0", {"start": v(70.52, -60.56) * mm, "mid": v(70.52, -57.06) * mm, "end": v(67.01, -57.06) * mm});
            skLineSegment(sketch, "E43.25.8.0", {"start": v(62.8, -68.28) * mm, "end": v(70.52, -60.56) * mm});
            skLineSegment(sketch, "E43.28.8.0", {"start": v(48.2, -75.87) * mm, "end": v(55.92, -68.15) * mm, "construction": true});
            skLineSegment(sketch, "E43.31.8.0", {"start": v(48.2, -60.42) * mm, "end": v(55.92, -68.15) * mm, "construction": true});
            skLineSegment(sketch, "E43.34.8.0", {"start": v(51.57, -57.06) * mm, "end": v(59.3, -64.78) * mm});
            skLineSegment(sketch, "E43.37.8.0", {"start": v(67.01, -57.06) * mm, "end": v(59.3, -64.78) * mm, "construction": true});
            skLineSegment(sketch, "E43.40.8.0", {"start": v(67.01, -79.24) * mm, "end": v(59.3, -71.52) * mm});
            skLineSegment(sketch, "E43.43.8.0", {"start": v(62.8, -68.28) * mm, "end": v(70.52, -76) * mm});
            skLineSegment(sketch, "E43.46.8.0", {"start": v(59.3, -64.78) * mm, "end": v(67.01, -57.06) * mm});
            skLineSegment(sketch, "E43.49.8.0", {"start": v(55.92, -68.15) * mm, "end": v(48.2, -75.87) * mm});
            skLineSegment(sketch, "E43.52.8.0", {"start": v(48.2, -60.42) * mm, "end": v(55.92, -68.15) * mm});
            skLineSegment(sketch, "E43.55.8.0", {"start": v(59.3, -71.52) * mm, "end": v(51.57, -79.24) * mm});
            skArc(sketch, "E43.0.9.0", {"start": v(87.82, -75.87) * mm, "mid": v(87.82, -79.24) * mm, "end": v(91.2, -79.24) * mm});
            skArc(sketch, "E43.4.9.0", {"start": v(91.2, -57.06) * mm, "mid": v(87.82, -57.06) * mm, "end": v(87.82, -60.42) * mm});
            skLineSegment(sketch, "E43.8.9.0", {"start": v(102.42, -68.28) * mm, "end": v(110.14, -76) * mm, "construction": true});
            skLineSegment(sketch, "E43.11.9.0", {"start": v(98.91, -71.52) * mm, "end": v(106.64, -79.24) * mm, "construction": true});
            skLineSegment(sketch, "E43.14.9.0", {"start": v(91.2, -79.24) * mm, "end": v(98.91, -71.52) * mm, "construction": true});
            skArc(sketch, "E43.17.9.0", {"start": v(106.64, -79.24) * mm, "mid": v(110, -79.37) * mm, "end": v(110.14, -76) * mm});
            skArc(sketch, "E43.21.9.0", {"start": v(110.14, -60.56) * mm, "mid": v(110.14, -57.06) * mm, "end": v(106.64, -57.06) * mm});
            skLineSegment(sketch, "E43.25.9.0", {"start": v(102.42, -68.28) * mm, "end": v(110.14, -60.56) * mm});
            skLineSegment(sketch, "E43.28.9.0", {"start": v(87.82, -75.87) * mm, "end": v(95.55, -68.15) * mm, "construction": true});
            skLineSegment(sketch, "E43.31.9.0", {"start": v(87.82, -60.42) * mm, "end": v(95.55, -68.15) * mm, "construction": true});
            skLineSegment(sketch, "E43.34.9.0", {"start": v(91.2, -57.06) * mm, "end": v(98.91, -64.78) * mm});
            skLineSegment(sketch, "E43.37.9.0", {"start": v(106.64, -57.06) * mm, "end": v(98.91, -64.78) * mm, "construction": true});
            skLineSegment(sketch, "E43.40.9.0", {"start": v(106.64, -79.24) * mm, "end": v(98.91, -71.52) * mm});
            skLineSegment(sketch, "E43.43.9.0", {"start": v(102.42, -68.28) * mm, "end": v(110.14, -76) * mm});
            skLineSegment(sketch, "E43.46.9.0", {"start": v(98.91, -64.78) * mm, "end": v(106.64, -57.06) * mm});
            skLineSegment(sketch, "E43.49.9.0", {"start": v(95.55, -68.15) * mm, "end": v(87.82, -75.87) * mm});
            skLineSegment(sketch, "E43.52.9.0", {"start": v(87.82, -60.42) * mm, "end": v(95.55, -68.15) * mm});
            skLineSegment(sketch, "E43.55.9.0", {"start": v(98.91, -71.52) * mm, "end": v(91.2, -79.24) * mm});
            skArc(sketch, "E44.0.1.1", {"start": v(110.14, -20.94) * mm, "mid": v(110.14, -17.43) * mm, "end": v(106.64, -17.43) * mm});
            skLineSegment(sketch, "E44.0.1.2", {"start": v(91.2, -39.61) * mm, "end": v(98.91, -31.9) * mm, "construction": true});
            skLineSegment(sketch, "E44.0.1.3", {"start": v(106.64, -17.43) * mm, "end": v(98.91, -25.16) * mm, "construction": true});
            skLineSegment(sketch, "E44.0.1.4", {"start": v(102.42, -28.66) * mm, "end": v(110.14, -20.94) * mm});
            skLineSegment(sketch, "E44.0.1.5", {"start": v(87.82, -36.25) * mm, "end": v(95.55, -28.52) * mm, "construction": true});
            skLineSegment(sketch, "E44.0.1.6", {"start": v(87.82, -20.8) * mm, "end": v(95.55, -28.52) * mm, "construction": true});
            skLineSegment(sketch, "E44.0.1.7", {"start": v(102.42, -28.66) * mm, "end": v(110.14, -36.38) * mm, "construction": true});
            skLineSegment(sketch, "E44.0.1.8", {"start": v(91.2, -17.43) * mm, "end": v(98.91, -25.16) * mm});
            skArc(sketch, "E44.0.1.9", {"start": v(91.2, -17.43) * mm, "mid": v(87.82, -17.43) * mm, "end": v(87.82, -20.8) * mm});
            skLineSegment(sketch, "E44.0.1.10", {"start": v(98.91, -31.9) * mm, "end": v(106.64, -39.61) * mm, "construction": true});
            skLineSegment(sketch, "E44.0.1.11", {"start": v(87.82, -20.8) * mm, "end": v(95.55, -28.52) * mm});
            skLineSegment(sketch, "E44.0.1.12", {"start": v(98.91, -25.16) * mm, "end": v(106.64, -17.43) * mm});
            skLineSegment(sketch, "E44.0.1.13", {"start": v(95.55, -28.52) * mm, "end": v(87.82, -36.25) * mm});
            skLineSegment(sketch, "E44.0.1.14", {"start": v(98.91, -31.9) * mm, "end": v(91.2, -39.61) * mm});
            skArc(sketch, "E44.0.1.15", {"start": v(87.82, -36.25) * mm, "mid": v(87.82, -39.61) * mm, "end": v(91.2, -39.61) * mm});
            skArc(sketch, "E44.0.1.16", {"start": v(106.64, -39.61) * mm, "mid": v(110, -39.75) * mm, "end": v(110.14, -36.38) * mm});
            skLineSegment(sketch, "E44.0.1.17", {"start": v(106.64, -39.61) * mm, "end": v(98.91, -31.9) * mm});
            skLineSegment(sketch, "E44.0.1.18", {"start": v(102.42, -28.66) * mm, "end": v(110.14, -36.38) * mm});
            skArc(sketch, "E44.0.2.1", {"start": v(110.14, 18.69) * mm, "mid": v(110.14, 22.2) * mm, "end": v(106.64, 22.2) * mm});
            skLineSegment(sketch, "E44.0.2.2", {"start": v(91.2, 0) * mm, "end": v(98.91, 7.73) * mm, "construction": true});
            skLineSegment(sketch, "E44.0.2.3", {"start": v(106.64, 22.2) * mm, "end": v(98.91, 14.47) * mm, "construction": true});
            skLineSegment(sketch, "E44.0.2.4", {"start": v(102.42, 10.97) * mm, "end": v(110.14, 18.69) * mm});
            skLineSegment(sketch, "E44.0.2.5", {"start": v(87.82, 3.38) * mm, "end": v(95.55, 11.1) * mm, "construction": true});
            skLineSegment(sketch, "E44.0.2.6", {"start": v(87.82, 18.82) * mm, "end": v(95.55, 11.1) * mm, "construction": true});
            skLineSegment(sketch, "E44.0.2.7", {"start": v(102.42, 10.97) * mm, "end": v(110.14, 3.24) * mm, "construction": true});
            skLineSegment(sketch, "E44.0.2.8", {"start": v(91.2, 22.2) * mm, "end": v(98.91, 14.47) * mm});
            skArc(sketch, "E44.0.2.9", {"start": v(91.2, 22.2) * mm, "mid": v(87.82, 22.2) * mm, "end": v(87.82, 18.82) * mm});
            skLineSegment(sketch, "E44.0.2.10", {"start": v(98.91, 7.73) * mm, "end": v(106.64, 0) * mm, "construction": true});
            skLineSegment(sketch, "E44.0.2.11", {"start": v(87.82, 18.82) * mm, "end": v(95.55, 11.1) * mm});
            skLineSegment(sketch, "E44.0.2.12", {"start": v(98.91, 14.47) * mm, "end": v(106.64, 22.2) * mm});
            skLineSegment(sketch, "E44.0.2.13", {"start": v(95.55, 11.1) * mm, "end": v(87.82, 3.38) * mm});
            skLineSegment(sketch, "E44.0.2.14", {"start": v(98.91, 7.73) * mm, "end": v(91.2, 0) * mm});
            skArc(sketch, "E44.0.2.15", {"start": v(87.82, 3.38) * mm, "mid": v(87.82, 0) * mm, "end": v(91.2, 0) * mm});
            skArc(sketch, "E44.0.2.16", {"start": v(106.64, 0) * mm, "mid": v(110, -0.13) * mm, "end": v(110.14, 3.24) * mm});
            skLineSegment(sketch, "E44.0.2.17", {"start": v(106.64, 0) * mm, "end": v(98.91, 7.73) * mm});
            skLineSegment(sketch, "E44.0.2.18", {"start": v(102.42, 10.97) * mm, "end": v(110.14, 3.24) * mm});
            skArc(sketch, "E44.0.3.1", {"start": v(110.14, 58.31) * mm, "mid": v(110.14, 61.81) * mm, "end": v(106.64, 61.81) * mm});
            skLineSegment(sketch, "E44.0.3.2", {"start": v(91.2, 39.63) * mm, "end": v(98.91, 47.36) * mm, "construction": true});
            skLineSegment(sketch, "E44.0.3.3", {"start": v(106.64, 61.81) * mm, "end": v(98.91, 54.1) * mm, "construction": true});
            skLineSegment(sketch, "E44.0.3.4", {"start": v(102.42, 50.59) * mm, "end": v(110.14, 58.31) * mm});
            skLineSegment(sketch, "E44.0.3.5", {"start": v(87.82, 43) * mm, "end": v(95.55, 50.72) * mm, "construction": true});
            skLineSegment(sketch, "E44.0.3.6", {"start": v(87.82, 58.45) * mm, "end": v(95.55, 50.72) * mm, "construction": true});
            skLineSegment(sketch, "E44.0.3.7", {"start": v(102.42, 50.59) * mm, "end": v(110.14, 42.87) * mm, "construction": true});
            skLineSegment(sketch, "E44.0.3.8", {"start": v(91.2, 61.81) * mm, "end": v(98.91, 54.1) * mm});
            skArc(sketch, "E44.0.3.9", {"start": v(91.2, 61.81) * mm, "mid": v(87.82, 61.81) * mm, "end": v(87.82, 58.45) * mm});
            skLineSegment(sketch, "E44.0.3.10", {"start": v(98.91, 47.36) * mm, "end": v(106.64, 39.63) * mm, "construction": true});
            skLineSegment(sketch, "E44.0.3.11", {"start": v(87.82, 58.45) * mm, "end": v(95.55, 50.72) * mm});
            skLineSegment(sketch, "E44.0.3.12", {"start": v(98.91, 54.1) * mm, "end": v(106.64, 61.81) * mm});
            skLineSegment(sketch, "E44.0.3.13", {"start": v(95.55, 50.72) * mm, "end": v(87.82, 43) * mm});
            skLineSegment(sketch, "E44.0.3.14", {"start": v(98.91, 47.36) * mm, "end": v(91.2, 39.63) * mm});
            skArc(sketch, "E44.0.3.15", {"start": v(87.82, 43) * mm, "mid": v(87.82, 39.63) * mm, "end": v(91.2, 39.63) * mm});
            skArc(sketch, "E44.0.3.16", {"start": v(106.64, 39.63) * mm, "mid": v(110, 39.5) * mm, "end": v(110.14, 42.87) * mm});
            skLineSegment(sketch, "E44.0.3.17", {"start": v(106.64, 39.63) * mm, "end": v(98.91, 47.36) * mm});
            skLineSegment(sketch, "E44.0.3.18", {"start": v(102.42, 50.59) * mm, "end": v(110.14, 42.87) * mm});
            skSolve(sketch);
        }
        {
            var Q0;
            Q0=qSketchRegion(id+"F10",true);
            extrude(context, id + "F11", {"entities" : qUnion([Q0]), "operationType" : NewBodyOperationType.REMOVE, "oppositeDirection" : true, "depth" : 1.9 * mm, "offsetDistance" : 25.4 * mm});
        }
    });
